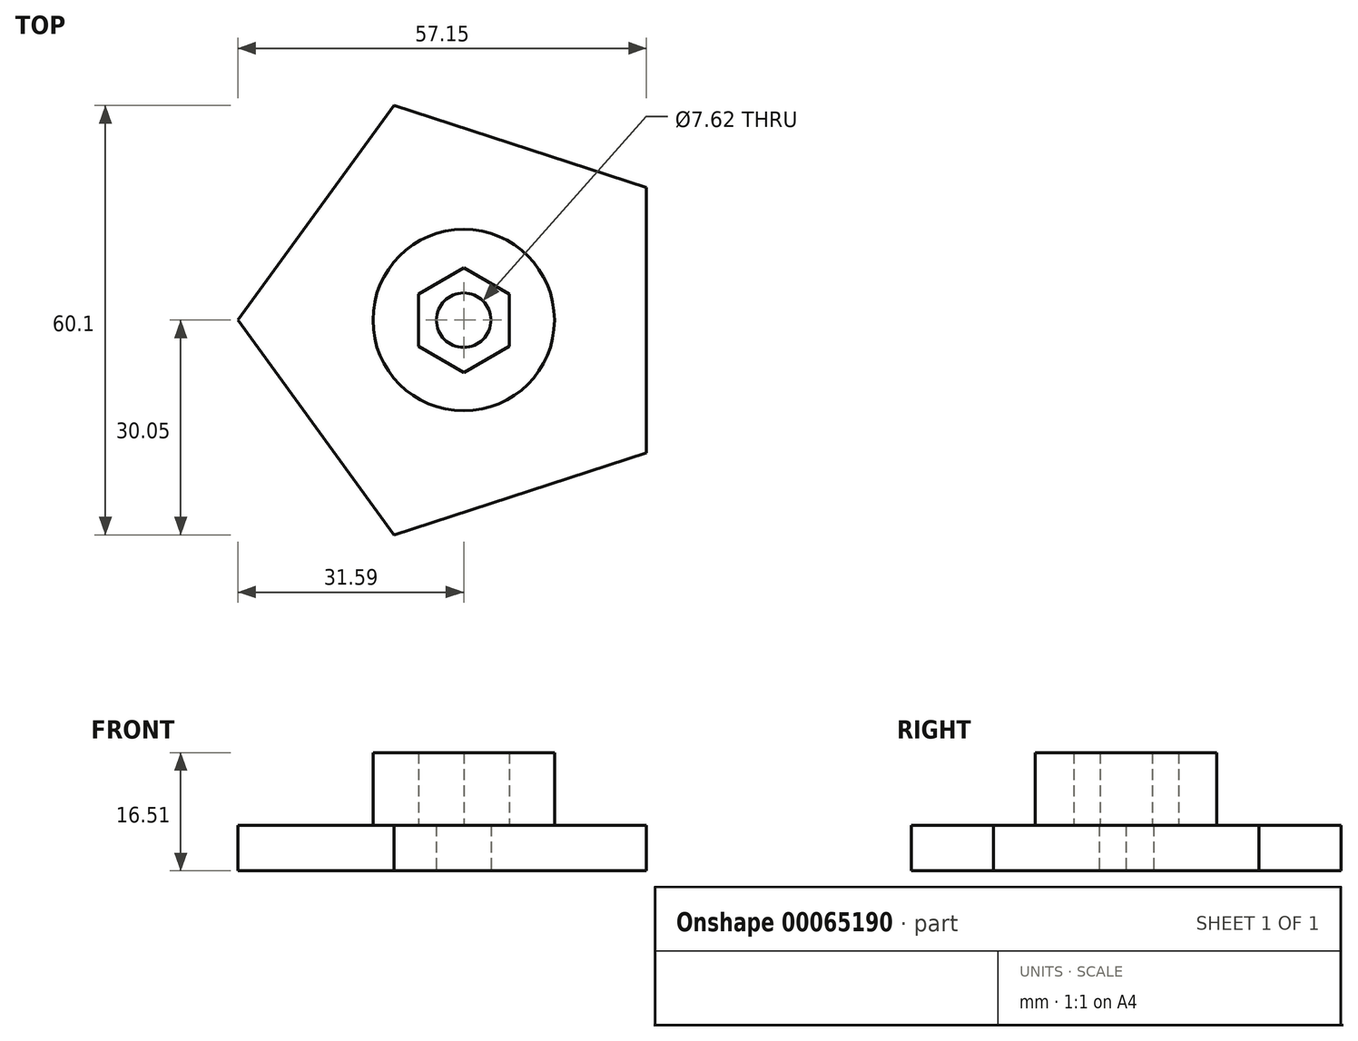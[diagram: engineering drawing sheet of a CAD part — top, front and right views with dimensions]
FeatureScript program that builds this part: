
annotation { "Feature Type Name" : "Feature", "Feature Type Description" : "" }
export const myFeature = defineFeature(function(context is Context, id is Id, definition is map)
    precondition{}
    {
        {
            var Q0;
            Q0=qCreatedBy(makeId("Top.planeOp"),FACE);
            var sketch = newSketch(context, id + "F0", { "sketchPlane" : qUnion([Q0])});
            skCircle(sketch, "E0.cCircle", {"center": v(0, 0) * mm, "radius": 25.56 * mm, "construction": true});
            skLineSegment(sketch, "E0.0", {"start": v(25.56, 18.57) * mm, "end": v(25.56, -18.57) * mm});
            skLineSegment(sketch, "E0.1", {"start": v(25.56, -18.57) * mm, "end": v(-9.76, -30.05) * mm});
            skLineSegment(sketch, "E0.2", {"start": v(-9.76, -30.05) * mm, "end": v(-31.6, 0) * mm});
            skLineSegment(sketch, "E0.3", {"start": v(-31.6, 0) * mm, "end": v(-9.76, 30.05) * mm});
            skLineSegment(sketch, "E0.4", {"start": v(-9.76, 30.05) * mm, "end": v(25.56, 18.57) * mm});
            skPoint(sketch, "E0.0.midPoint", {"position": v(25.56, 0) * mm});
            skSolve(sketch);
        }
        {
            var Q0;
            Q0=makeQuery(id+"F0.imprint","IMPRINT",FACE,{"disambiguationData":[TD([[makeQuery(id+"F0.imprint","IMPRINT",EDGE,{"derivedFrom":sQuery(id+"F0.wireOp",EDGE,"E0.0")}),-1.0]])]});
            extrude(context, id + "F1", {"entities" : qUnion([Q0]), "depth" : 6.35 * mm});
        }
        {
            var Q0;
            Q0=makeQuery(id+"F1.opExtrude","CAP_FACE",FACE,{"disambiguationData":[OSD([sQuery(id+"F0.wireOp",EDGE,"E0.0"),sQuery(id+"F0.wireOp",EDGE,"E0.1"),sQuery(id+"F0.wireOp",EDGE,"E0.2"),sQuery(id+"F0.wireOp",EDGE,"E0.3"),sQuery(id+"F0.wireOp",EDGE,"E0.4")])],"isStart":false});
            var sketch = newSketch(context, id + "F2", { "sketchPlane" : qUnion([Q0])});
            skCircle(sketch, "E1.cCircle", {"center": v(0, 0) * mm, "radius": 6.35 * mm, "construction": true});
            skLineSegment(sketch, "E1.0", {"start": v(6.35, 3.67) * mm, "end": v(6.35, -3.67) * mm});
            skLineSegment(sketch, "E1.1", {"start": v(6.35, -3.67) * mm, "end": v(0, -7.33) * mm});
            skLineSegment(sketch, "E1.2", {"start": v(0, -7.33) * mm, "end": v(-6.35, -3.67) * mm});
            skLineSegment(sketch, "E1.3", {"start": v(-6.35, -3.67) * mm, "end": v(-6.35, 3.67) * mm});
            skLineSegment(sketch, "E1.4", {"start": v(-6.35, 3.67) * mm, "end": v(0, 7.33) * mm});
            skLineSegment(sketch, "E1.5", {"start": v(0, 7.33) * mm, "end": v(6.35, 3.67) * mm});
            skPoint(sketch, "E1.0.midPoint", {"position": v(6.35, 0) * mm});
            skCircle(sketch, "E2", {"center": v(0, 0) * mm, "radius": 12.7 * mm});
            skSolve(sketch);
        }
        {
            var Q0;
            Q0=makeQuery(id+"F2.imprint","IMPRINT",FACE,{"disambiguationData":[TD([[makeQuery(id+"F2.imprint","IMPRINT",EDGE,{"derivedFrom":sQuery(id+"F2.wireOp",EDGE,"E1.0")}),1.0]])]});
            extrude(context, id + "F3", {"entities" : qUnion([Q0]), "operationType" : NewBodyOperationType.ADD, "depth" : 10.16 * mm});
        }
        {
            var Q0;
            Q0=makeQuery(id+"F1.opExtrude","CAP_FACE",FACE,{"disambiguationData":[OSD([sQuery(id+"F0.wireOp",EDGE,"E0.0"),sQuery(id+"F0.wireOp",EDGE,"E0.1"),sQuery(id+"F0.wireOp",EDGE,"E0.2"),sQuery(id+"F0.wireOp",EDGE,"E0.3"),sQuery(id+"F0.wireOp",EDGE,"E0.4")])],"isStart":true});
            var sketch = newSketch(context, id + "F4", { "sketchPlane" : qUnion([Q0])});
            skCircle(sketch, "E3", {"center": v(0, 0) * mm, "radius": 3.8 * mm});
            skSolve(sketch);
        }
        {
            var Q0;
            Q0=makeQuery(id+"F4.imprint","IMPRINT",FACE,{"disambiguationData":[TD([[makeQuery(id+"F4.imprint","IMPRINT",EDGE,{"derivedFrom":sQuery(id+"F4.wireOp",EDGE,"E3")}),1.0]])]});
            extrude(context, id + "F5", {"entities" : qUnion([Q0]), "operationType" : NewBodyOperationType.REMOVE, "oppositeDirection" : true, "depth" : 25.4 * mm});
        }
    });
